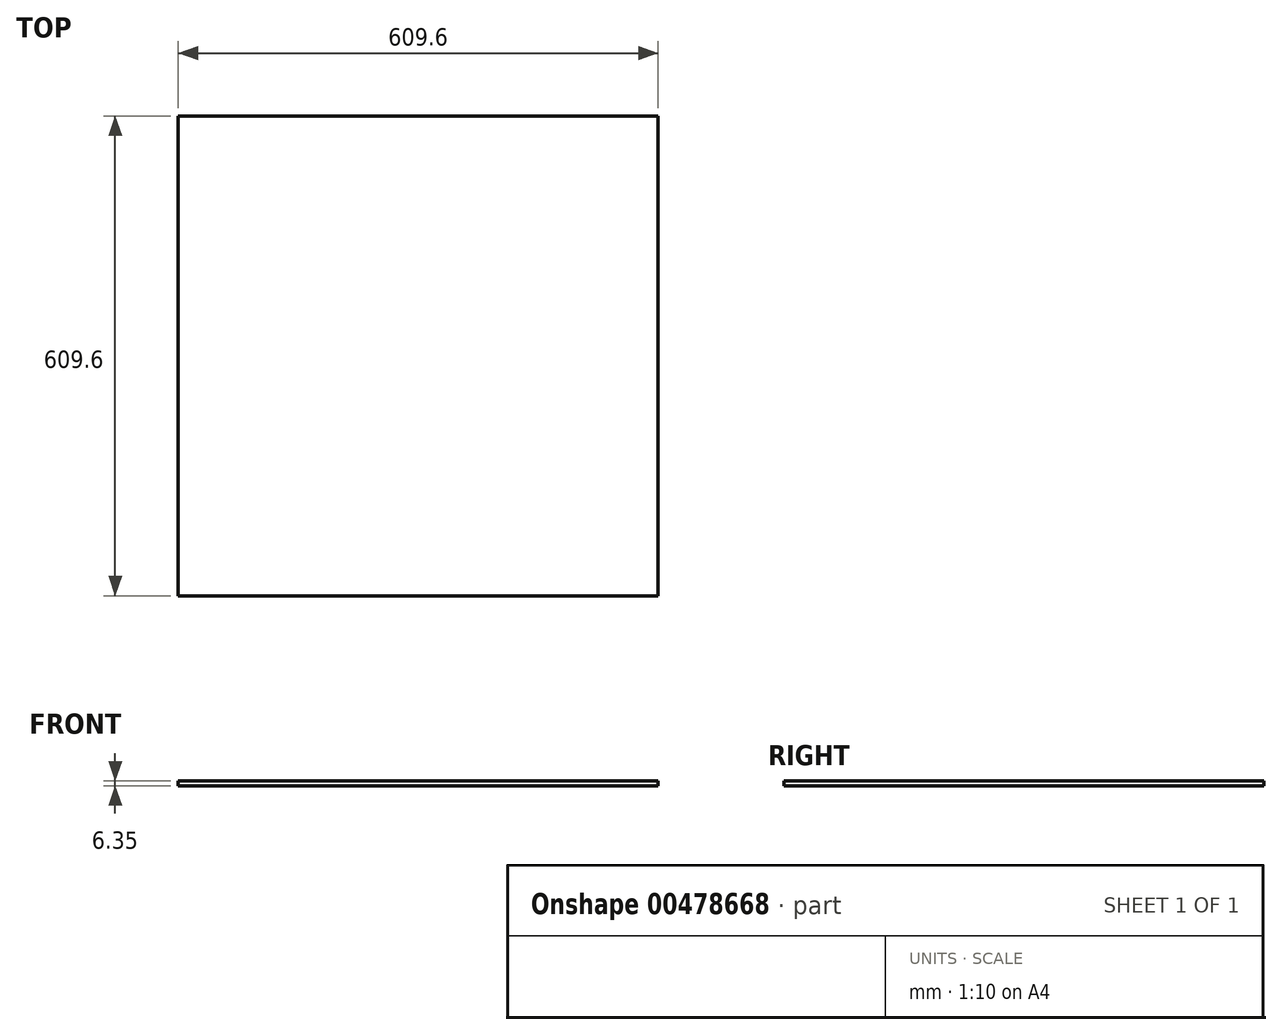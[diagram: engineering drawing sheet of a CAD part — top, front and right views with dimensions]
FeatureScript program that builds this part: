
annotation { "Feature Type Name" : "Feature", "Feature Type Description" : "" }
export const myFeature = defineFeature(function(context is Context, id is Id, definition is map)
    precondition{}
    {
        {
            var Q0;
            Q0=qCreatedBy(makeId("Top.planeOp"),FACE);
            var sketch = newSketch(context, id + "F0", { "sketchPlane" : qUnion([Q0])});
            skLineSegment(sketch, "E0.bottom", {"start": v(-48.9, -41.46) * mm, "end": v(560.7, -41.46) * mm});
            skLineSegment(sketch, "E0.top", {"start": v(-48.9, 568.14) * mm, "end": v(560.7, 568.14) * mm});
            skLineSegment(sketch, "E0.left", {"start": v(-48.9, -41.46) * mm, "end": v(-48.9, 568.14) * mm});
            skLineSegment(sketch, "E0.right", {"start": v(560.7, -41.46) * mm, "end": v(560.7, 568.14) * mm});
            skPoint(sketch, "E0.middle", {"position": v(255.9, 263.34) * mm});
            skSolve(sketch);
        }
        {
            var Q0;
            Q0=makeQuery(id+"F0.imprint","IMPRINT",FACE,{"disambiguationData":[TD([[makeQuery(id+"F0.imprint","IMPRINT",EDGE,{"derivedFrom":sQuery(id+"F0.wireOp",EDGE,"E0.bottom")}),1.0]])]});
            extrude(context, id + "F1", {"entities" : qUnion([Q0]), "depth" : 6.35 * mm});
        }
    });
